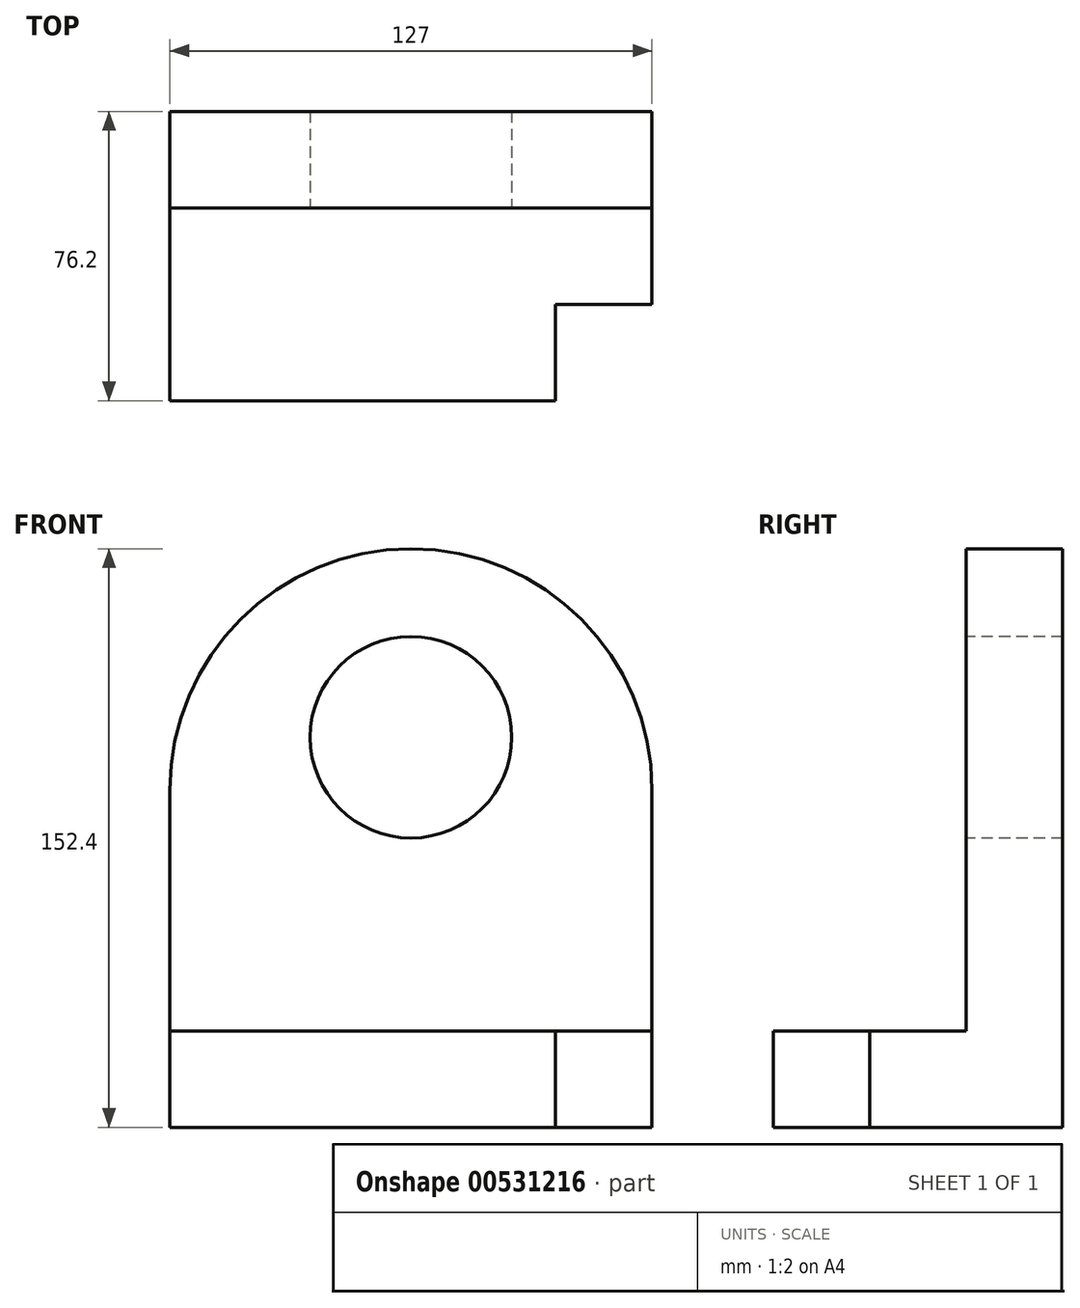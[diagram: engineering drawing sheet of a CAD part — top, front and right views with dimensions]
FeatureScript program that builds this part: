
annotation { "Feature Type Name" : "Feature", "Feature Type Description" : "" }
export const myFeature = defineFeature(function(context is Context, id is Id, definition is map)
    precondition{}
    {
        {
            var Q0;
            Q0=qCreatedBy(makeId("Top.planeOp"),FACE);
            var sketch = newSketch(context, id + "F0", { "sketchPlane" : qUnion([Q0])});
            skLineSegment(sketch, "E0.bottom", {"start": v(63.5, 38.1) * mm, "end": v(-63.5, 38.1) * mm});
            skLineSegment(sketch, "E0.top", {"start": v(63.5, -38.1) * mm, "end": v(-63.5, -38.1) * mm});
            skLineSegment(sketch, "E0.left", {"start": v(63.5, 38.1) * mm, "end": v(63.5, -38.1) * mm});
            skLineSegment(sketch, "E0.right", {"start": v(-63.5, 38.1) * mm, "end": v(-63.5, -38.1) * mm});
            skPoint(sketch, "E0.middle", {"position": v(0, 0) * mm});
            skLineSegment(sketch, "E1.bottom", {"start": v(63.5, -38.1) * mm, "end": v(38.1, -38.1) * mm});
            skLineSegment(sketch, "E1.top", {"start": v(63.5, -12.7) * mm, "end": v(38.1, -12.7) * mm});
            skLineSegment(sketch, "E1.left", {"start": v(63.5, -38.1) * mm, "end": v(63.5, -12.7) * mm});
            skLineSegment(sketch, "E1.right", {"start": v(38.1, -38.1) * mm, "end": v(38.1, -12.7) * mm});
            skSolve(sketch);
        }
        {
            var Q0;
            Q0=makeQuery(id+"F0.imprint","IMPRINT",FACE,{"disambiguationData":[TD([[makeQuery(id+"F0.imprint","IMPRINT",EDGE,{"derivedFrom":sQuery(id+"F0.wireOp",EDGE,"E0.bottom")}),1.0]])]});
            extrude(context, id + "F1", {"entities" : qUnion([Q0]), "depth" : 25.4 * mm, "offsetDistance" : 25.4 * mm});
        }
        {
            var Q0;
            Q0=makeQuery(id+"F1.opExtrude","CAP_FACE",FACE,{"disambiguationData":[OSD([sQuery(id+"F0.wireOp",EDGE,"E0.bottom"),sQuery(id+"F0.wireOp",EDGE,"E0.top"),sQuery(id+"F0.wireOp",EDGE,"E0.left"),sQuery(id+"F0.wireOp",EDGE,"E0.right"),sQuery(id+"F0.wireOp",EDGE,"E1.top"),sQuery(id+"F0.wireOp",EDGE,"E1.right")])],"isStart":false});
            var sketch = newSketch(context, id + "F2", { "sketchPlane" : qUnion([Q0])});
            skLineSegment(sketch, "E2.bottom", {"start": v(63.5, 38.1) * mm, "end": v(-63.5, 38.1) * mm});
            skLineSegment(sketch, "E2.top", {"start": v(63.5, 12.7) * mm, "end": v(-63.5, 12.7) * mm});
            skLineSegment(sketch, "E2.left", {"start": v(63.5, 38.1) * mm, "end": v(63.5, 12.7) * mm});
            skLineSegment(sketch, "E2.right", {"start": v(-63.5, 38.1) * mm, "end": v(-63.5, 12.7) * mm});
            skSolve(sketch);
        }
        {
            var Q0;
            Q0=makeQuery(id+"F2.imprint","IMPRINT",FACE,{"disambiguationData":[TD([[makeQuery(id+"F2.imprint","IMPRINT",EDGE,{"derivedFrom":sQuery(id+"F2.wireOp",EDGE,"E2.bottom")}),1.0]])]});
            extrude(context, id + "F3", {"entities" : qUnion([Q0]), "operationType" : NewBodyOperationType.ADD, "depth" : 127 * mm, "offsetDistance" : 25.4 * mm});
        }
        {
            var Q0;
            Q0=makeQuery(id+"F3.opExtrude","CAP_EDGE",EDGE,{"disambiguationData":[OSD([sQuery(id+"F2.wireOp",EDGE,"E2.left")])],"isStart":false});
            fillet(context, id + "F4", {"entities" : qUnion([Q0]), "radius" : 63.5 * mm, "tangentPropagation" : true, "allowEdgeOverflow" : false});
        }
        {
            var Q0;
            Q0=makeQuery(id+"F3.opExtrude","CAP_EDGE",EDGE,{"disambiguationData":[OSD([sQuery(id+"F2.wireOp",EDGE,"E2.right")])],"isStart":false});
            fillet(context, id + "F5", {"entities" : qUnion([Q0]), "radius" : 63.5 * mm, "tangentPropagation" : true, "allowEdgeOverflow" : false});
        }
        {
            var Q0;
            Q0=makeQuery(id+"F3.opExtrude","SWEPT_FACE",FACE,{"disambiguationData":[OSD([sQuery(id+"F2.wireOp",EDGE,"E2.top")])]});
            var sketch = newSketch(context, id + "F6", { "sketchPlane" : qUnion([Q0])});
            skCircle(sketch, "E3", {"center": v(0, 102.75) * mm, "radius": 26.55 * mm});
            skSolve(sketch);
        }
        {
            var Q0;
            Q0=makeQuery(id+"F6.imprint","IMPRINT",FACE,{"disambiguationData":[TD([[makeQuery(id+"F6.imprint","IMPRINT",EDGE,{"derivedFrom":sQuery(id+"F6.wireOp",EDGE,"E3")}),1.0]])]});
            extrude(context, id + "F7", {"entities" : qUnion([Q0]), "operationType" : NewBodyOperationType.REMOVE, "endBound" : BoundingType.THROUGH_ALL, "oppositeDirection" : true, "depth" : 25.4 * mm, "offsetDistance" : 25.4 * mm});
        }
    });
